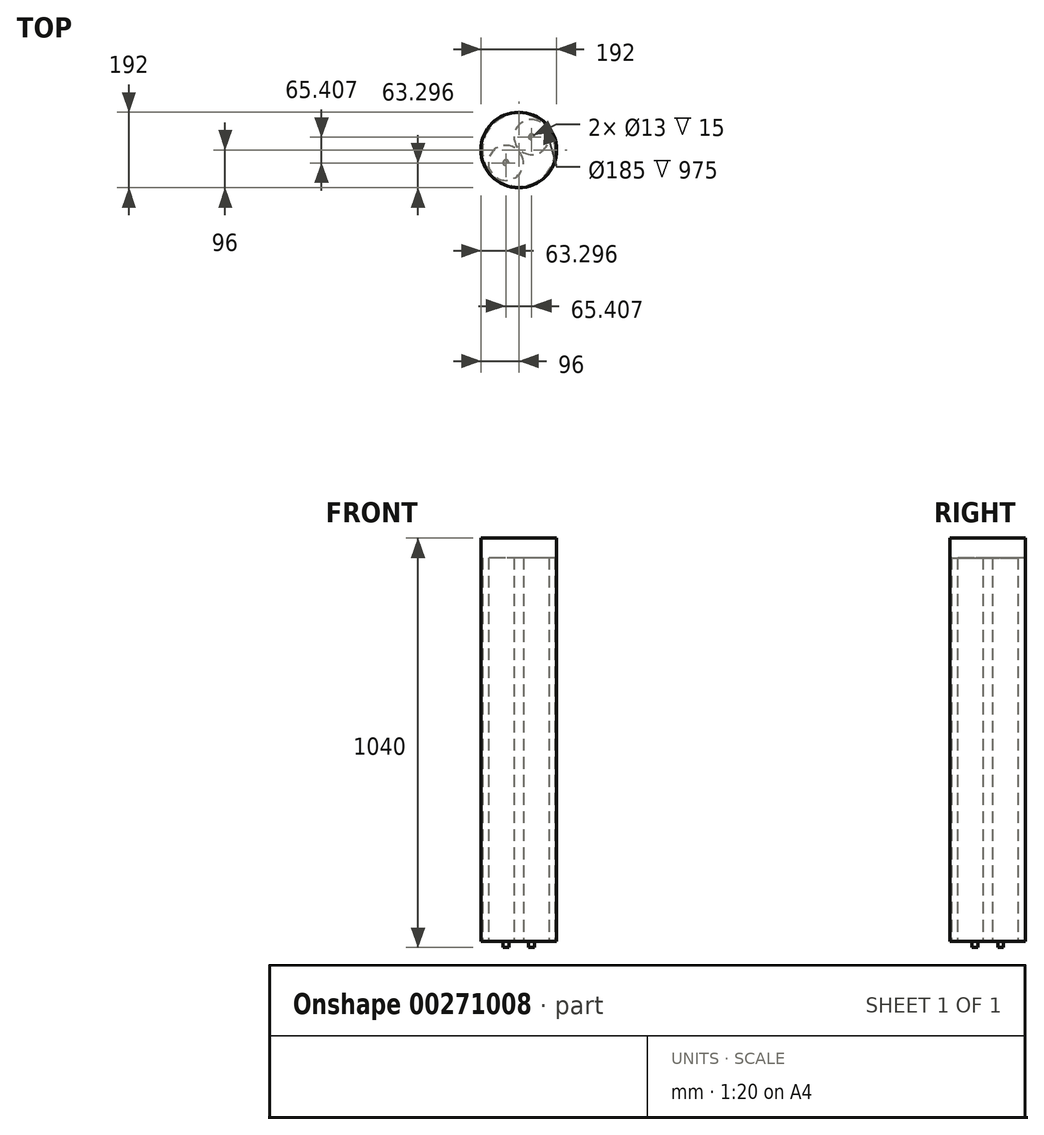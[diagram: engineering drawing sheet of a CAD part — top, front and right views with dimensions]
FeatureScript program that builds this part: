
annotation { "Feature Type Name" : "Feature", "Feature Type Description" : "" }
export const myFeature = defineFeature(function(context is Context, id is Id, definition is map)
    precondition{}
    {
        {
            var Q0;
            Q0=qCreatedBy(makeId("Top.planeOp"),FACE);
            var sketch = newSketch(context, id + "F0", { "sketchPlane" : qUnion([Q0])});
            skCircle(sketch, "E0", {"center": v(0, 0) * mm, "radius": 92.5 * mm});
            skCircle(sketch, "E1", {"center": v(-32.7, -32.7) * mm, "radius": 44.45 * mm});
            skCircle(sketch, "E2", {"center": v(32.7, 32.7) * mm, "radius": 44.45 * mm});
            skCircle(sketch, "E3", {"center": v(0, 0) * mm, "radius": 96 * mm});
            skSolve(sketch);
        }
        {
            var Q0;
            Q0=makeQuery(id+"F0.imprint","IMPRINT",FACE,{"disambiguationData":[TD([[makeQuery(id+"F0.imprint","IMPRINT",EDGE,{"derivedFrom":sQuery(id+"F0.wireOp",EDGE,"E1")}),1.0]])]});
            var Q1;
            Q1=makeQuery(id+"F0.imprint","IMPRINT",FACE,{"disambiguationData":[TD([[makeQuery(id+"F0.imprint","IMPRINT",EDGE,{"derivedFrom":sQuery(id+"F0.wireOp",EDGE,"E2")}),1.0]])]});
            var Q2;
            Q2=makeQuery(id+"F0.imprint","IMPRINT",FACE,{"disambiguationData":[TD([[makeQuery(id+"F0.imprint","IMPRINT",EDGE,{"derivedFrom":sQuery(id+"F0.wireOp",EDGE,"E0")}),-1.0]])]});
            extrude(context, id + "F1", {"entities" : qUnion([Q0, Q1, Q2]), "depth" : 1000 * mm});
        }
        {
            var Q0;
            Q0=makeQuery(id+"F1.opExtrude","CAP_FACE",FACE,{"disambiguationData":[OSD([sQuery(id+"F0.wireOp",EDGE,"E2")])],"isStart":true});
            var sketch = newSketch(context, id + "F2", { "sketchPlane" : qUnion([Q0])});
            skCircle(sketch, "E4", {"center": v(32.7, -32.7) * mm, "radius": 7.5 * mm});
            skCircle(sketch, "E5", {"center": v(32.7, -32.7) * mm, "radius": 6.5 * mm});
            skSolve(sketch);
        }
        {
            var Q0;
            Q0=makeQuery(id+"F2.imprint","IMPRINT",FACE,{"disambiguationData":[TD([[makeQuery(id+"F2.imprint","IMPRINT",EDGE,{"derivedFrom":sQuery(id+"F2.wireOp",EDGE,"E4")}),1.0]])]});
            extrude(context, id + "F3", {"entities" : qUnion([Q0]), "operationType" : NewBodyOperationType.ADD, "depth" : 15 * mm});
        }
        {
            var Q0;
            Q0=makeQuery(id+"F1.opExtrude","CAP_FACE",FACE,{"disambiguationData":[OSD([sQuery(id+"F0.wireOp",EDGE,"E0"),sQuery(id+"F0.wireOp",EDGE,"E3")])],"isStart":false});
            var sketch = newSketch(context, id + "F4", { "sketchPlane" : qUnion([Q0])});
            skCircle(sketch, "E6", {"center": v(0, 0) * mm, "radius": 96 * mm});
            skSolve(sketch);
        }
        {
            var Q0;
            Q0 = qSketchRegion(id + "F4", true);
            extrude(context, id + "F5", {"entities" : qUnion([Q0]), "operationType" : NewBodyOperationType.ADD, "depth" : 25 * mm, "hasSecondDirection" : true, "secondDirectionOppositeDirection" : true, "secondDirectionDepth" : 25 * mm});
        }
        {
            var Q0;
            Q0=makeQuery(id+"F1.opExtrude","CAP_FACE",FACE,{"disambiguationData":[OSD([sQuery(id+"F0.wireOp",EDGE,"E1")])],"isStart":true});
            var sketch = newSketch(context, id + "F6", { "sketchPlane" : qUnion([Q0])});
            skCircle(sketch, "E7", {"center": v(-32.7, 32.7) * mm, "radius": 7.5 * mm});
            skCircle(sketch, "E8", {"center": v(-32.7, 32.7) * mm, "radius": 6.5 * mm});
            skSolve(sketch);
        }
        {
            var Q0;
            Q0=makeQuery(id+"F6.imprint","IMPRINT",FACE,{"disambiguationData":[TD([[makeQuery(id+"F6.imprint","IMPRINT",EDGE,{"derivedFrom":sQuery(id+"F6.wireOp",EDGE,"E7")}),1.0]])]});
            extrude(context, id + "F7", {"entities" : qUnion([Q0]), "operationType" : NewBodyOperationType.ADD, "depth" : 15 * mm});
        }
        {
            var Q0;
            Q0=makeQuery(id+"F3.opExtrude","CAP_FACE",FACE,{"disambiguationData":[OSD([sQuery(id+"F2.wireOp",EDGE,"E4"),sQuery(id+"F2.wireOp",EDGE,"E5")])],"isStart":false});
            var sketch = newSketch(context, id + "F8", { "sketchPlane" : qUnion([Q0])});
            skLineSegment(sketch, "E9", {"start": v(32.7, -32.7) * mm, "end": v(-32.7, 32.7) * mm});
            skSolve(sketch);
        }
    });
